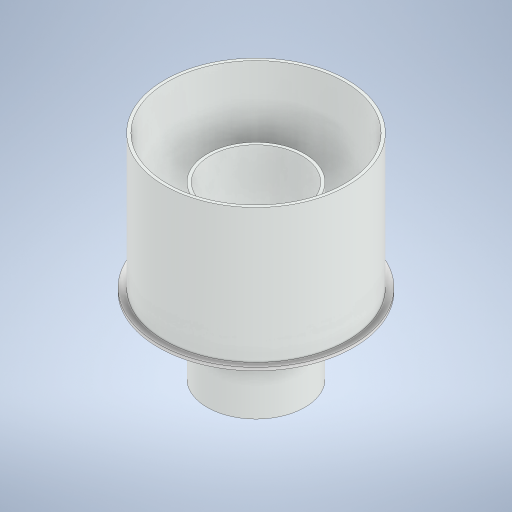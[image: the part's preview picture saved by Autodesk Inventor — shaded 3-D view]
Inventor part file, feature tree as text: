
AUTODESK INVENTOR PART (.ipt)
format: ipt  version: 2023.2 (Build 272271030, 271C)  size: 274,432 bytes
history: native  units: in
note: dims shown in document units (in); Inventor stores cm internally (conversion verified against a paired STEP export)
features: extrude x4, sketch x4
ambient origin geometry x8: Origin, YZ Plane, XZ Plane, XY Plane, X Axis, Y Axis, Z Axis, Center Point
bodies: Solid1 (feature_tree)
feature tree (8):
  extrude  "Extrusion1"  Depth=5.7087in
  extrude  "Extrusion2"  Depth=2.9528in
  extrude  "Extrusion3"  Depth=2.9528in TaperAngle=0.0deg
  extrude  "Extrusion4"  Depth=0.0984in TaperAngle=0.0deg
  sketch  "Sketch1"  dims[d0=5.9055in d1=5.7087in]
  sketch  "Sketch2"  dims[d2=4.3307in d3=0.0in d4=2.9528in]
  sketch  "Sketch3"  dims[d5=0.0984in d6=2.9528in d7=0.0in]
  sketch  "Sketch4"  dims[d8=6.2992in d9=0.0984in d10=0.0in d11=2.5591in d12=0.0in]
